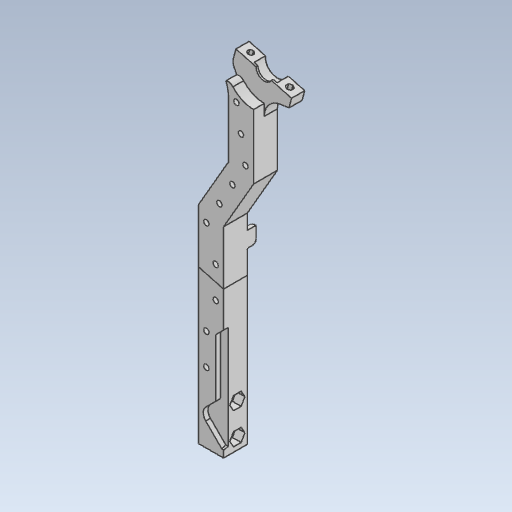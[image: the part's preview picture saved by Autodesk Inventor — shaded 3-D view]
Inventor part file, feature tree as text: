
AUTODESK INVENTOR PART (.ipt)
format: ipt  version: 2021.2 (Build 252289000, 289)  size: 381,952 bytes
history: native  units: mm
features: other x10, chamfer x2, fillet x1
ambient origin geometry x8: Origin, YZ Plane, XZ Plane, XY Plane, X Axis, Y Axis, Z Axis, Center Point
bodies: Body1 (feature_tree), Body2 (feature_tree)
feature tree (13):
  other  "Твёрдое тело.ipt"
  other  "РабПлоскость1"
  other  "Разделение1"
  fillet  "Сопряжение1"  Radius=10.0mm
  chamfer  "Фаска1"  Distance=1.0mm
  chamfer  "Фаска2"  Distance=2.0mm
  other  "Ножка 2::Твёрдое тело.ipt"
  other  "Элемент создания тегов1"
  other  "Ножка левая верх::Твёрдое тело.ipt"
  other  "Ножка левая низ::Твёрдое тело.ipt"
  other  "Твердое тело1"
  other  "Твердое тело2"
  other  "Твердое тело3"
